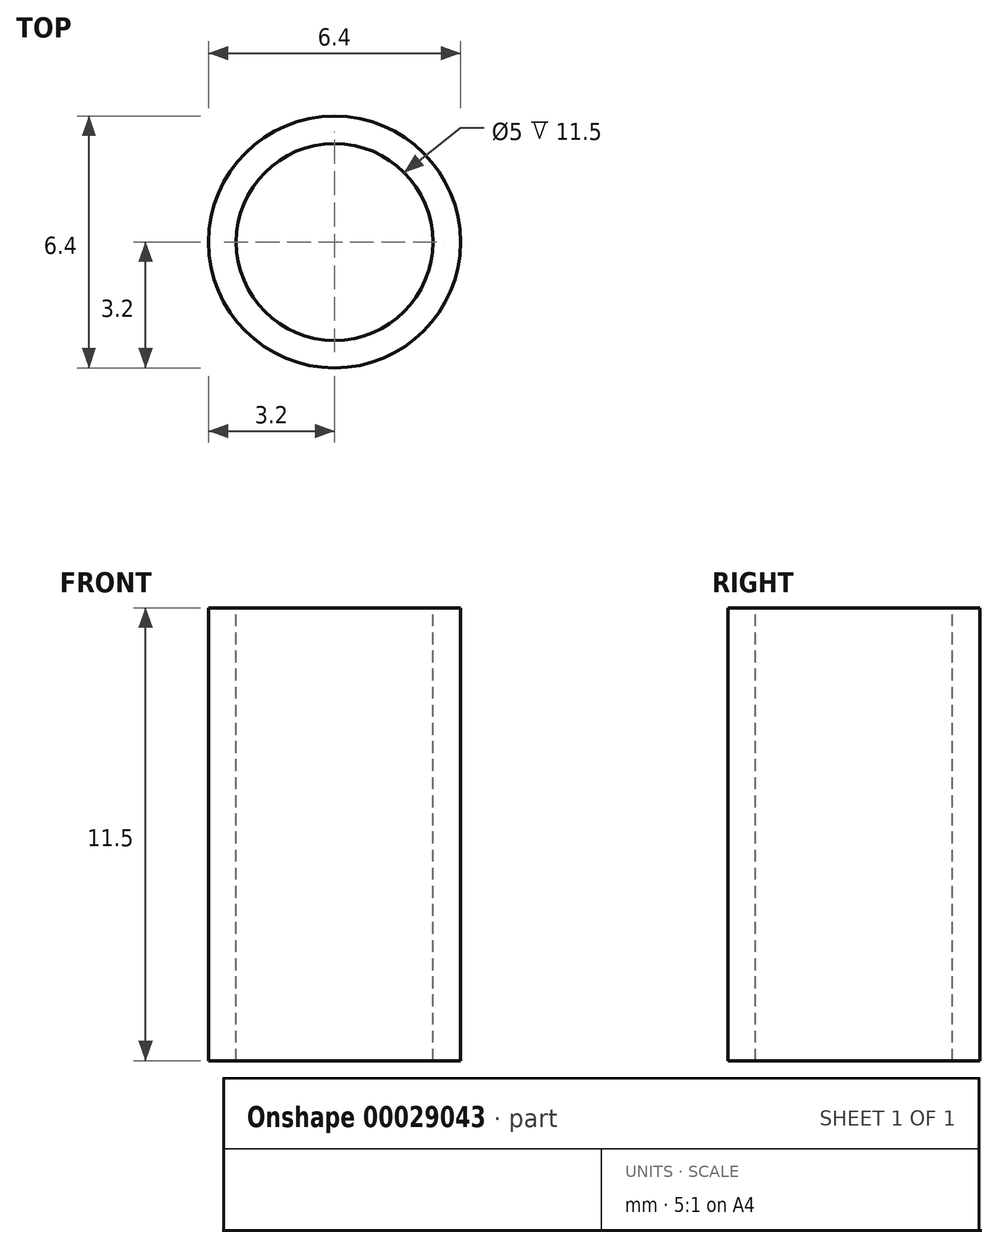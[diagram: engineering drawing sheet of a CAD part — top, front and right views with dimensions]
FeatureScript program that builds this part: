
annotation { "Feature Type Name" : "Feature", "Feature Type Description" : "" }
export const myFeature = defineFeature(function(context is Context, id is Id, definition is map)
    precondition{}
    {
        {
            var Q0;
            Q0=qCreatedBy(makeId("Top.planeOp"),FACE);
            var sketch = newSketch(context, id + "F0", { "sketchPlane" : qUnion([Q0])});
            skCircle(sketch, "E0", {"center": v(0, 0) * mm, "radius": 3.2 * mm});
            skSolve(sketch);
        }
        {
            var Q0;
            Q0=qSketchRegion(id+"F0",true);
            extrude(context, id + "F1", {"entities" : qUnion([Q0]), "depth" : 11.5 * mm});
        }
        {
            var Q0;
            Q0=makeQuery(id+"F1.opExtrude","CAP_FACE",FACE,{"disambiguationData":[OSD([sQuery(id+"F0.wireOp",EDGE,"E0")])],"isStart":false});
            var sketch = newSketch(context, id + "F2", { "sketchPlane" : qUnion([Q0])});
            skCircle(sketch, "E1", {"center": v(0, 0) * mm, "radius": 2.5 * mm});
            skSolve(sketch);
        }
        {
            var Q0;
            Q0=qSketchRegion(id+"F2",true);
            extrude(context, id + "F3", {"entities" : qUnion([Q0]), "operationType" : NewBodyOperationType.REMOVE, "endBound" : BoundingType.UP_TO_NEXT, "oppositeDirection" : true, "depth" : 25 * mm});
        }
    });
